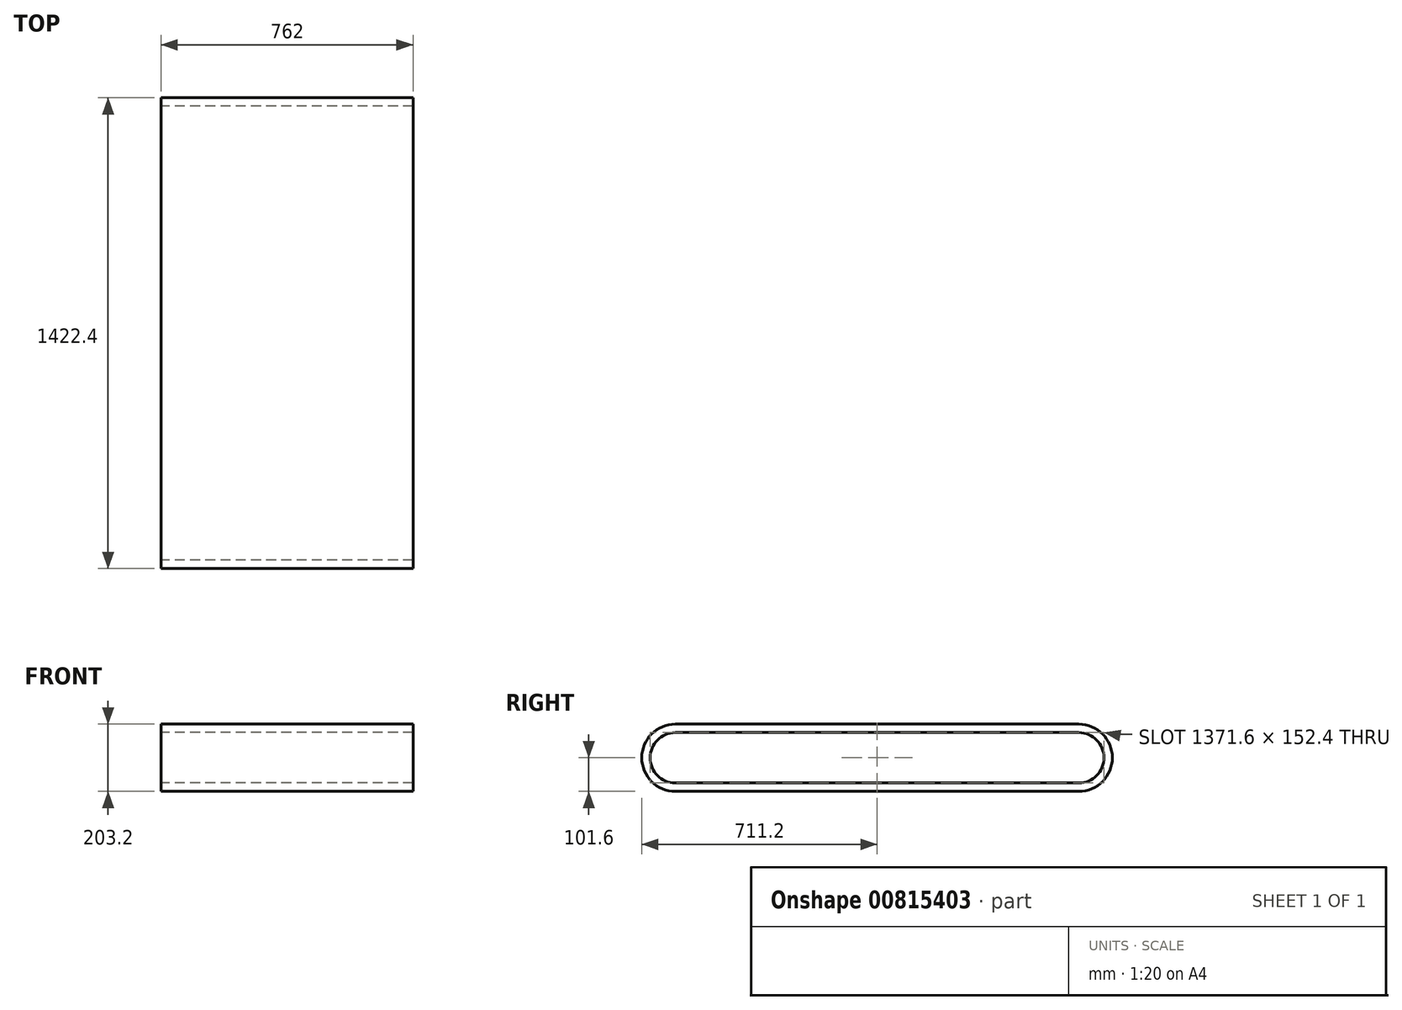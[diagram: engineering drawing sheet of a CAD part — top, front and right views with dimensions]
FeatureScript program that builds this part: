
annotation { "Feature Type Name" : "Feature", "Feature Type Description" : "" }
export const myFeature = defineFeature(function(context is Context, id is Id, definition is map)
    precondition{}
    {
        {
            var Q0;
            Q0=qCreatedBy(makeId("Right.planeOp"),FACE);
            var sketch = newSketch(context, id + "F0", { "sketchPlane" : qUnion([Q0])});
            skLineSegment(sketch, "E0", {"start": v(0, 0) * mm, "end": v(1219.2, 0) * mm});
            skArc(sketch, "E1.0.startCap", {"start": v(0, -76.2) * mm, "mid": v(-76.2, 0) * mm, "end": v(0, 76.2) * mm});
            skArc(sketch, "E1.0.endCap", {"start": v(1219.2, 76.2) * mm, "mid": v(1295.4, 0) * mm, "end": v(1219.2, -76.2) * mm});
            skLineSegment(sketch, "E1.0.left", {"start": v(0, 76.2) * mm, "end": v(1219.2, 76.2) * mm});
            skLineSegment(sketch, "E1.0.right", {"start": v(0, -76.2) * mm, "end": v(1219.2, -76.2) * mm});
            skLineSegment(sketch, "E2.0", {"start": v(0, -101.6) * mm, "end": v(1219.2, -101.6) * mm});
            skArc(sketch, "E2.1", {"start": v(0, -101.6) * mm, "mid": v(-101.6, 0) * mm, "end": v(0, 101.6) * mm});
            skLineSegment(sketch, "E2.2", {"start": v(0, 101.6) * mm, "end": v(1219.2, 101.6) * mm});
            skArc(sketch, "E2.3", {"start": v(1219.2, 101.6) * mm, "mid": v(1320.8, 0) * mm, "end": v(1219.2, -101.6) * mm});
            skSolve(sketch);
        }
        {
            var Q0;
            Q0 = qSketchRegion(id + "F0", true);
            extrude(context, id + "F1", {"entities" : qUnion([Q0]), "depth" : 762 * mm, "offsetDistance" : 25.4 * mm});
        }
    });
